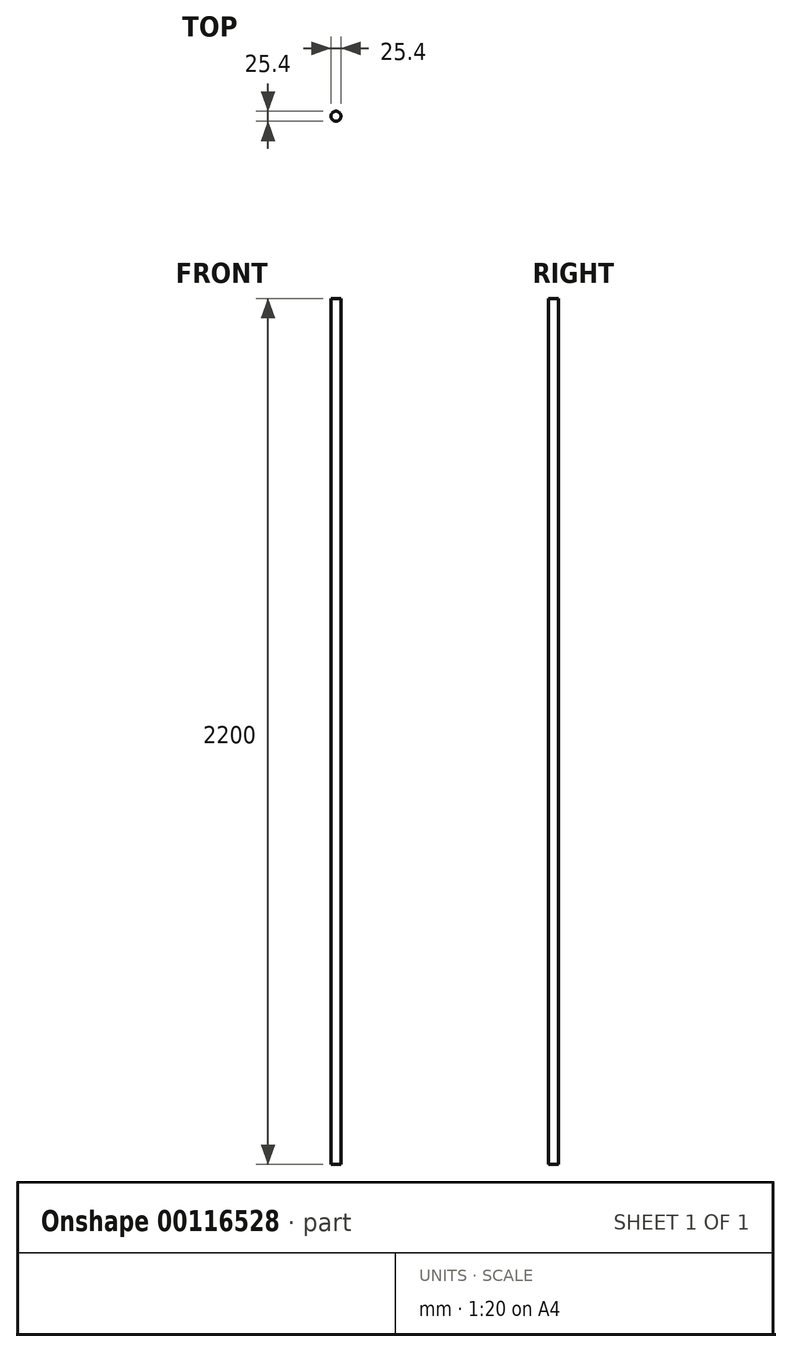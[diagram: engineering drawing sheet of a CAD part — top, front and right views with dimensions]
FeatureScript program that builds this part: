
annotation { "Feature Type Name" : "Feature", "Feature Type Description" : "" }
export const myFeature = defineFeature(function(context is Context, id is Id, definition is map)
    precondition{}
    {
        {
            var Q0;
            Q0=qCreatedBy(makeId("Top.planeOp"),FACE);
            var sketch = newSketch(context, id + "F0", { "sketchPlane" : qUnion([Q0])});
            skCircle(sketch, "E0", {"center": v(0, 0) * mm, "radius": 12.7 * mm});
            skSolve(sketch);
        }
        {
            var Q0;
            Q0 = qSketchRegion(id + "F0", true);
            var Q1;
            Q1=makeQuery(id+"F0.imprint","IMPRINT",FACE,{"disambiguationData":[TD([[makeQuery(id+"F0.imprint","IMPRINT",EDGE,{"derivedFrom":sQuery(id+"F0.wireOp",EDGE,"E0")}),1.0]])]});
            extrude(context, id + "F1", {"entities" : qUnion([Q0, Q1]), "depth" : 2200 * mm});
        }
    });
